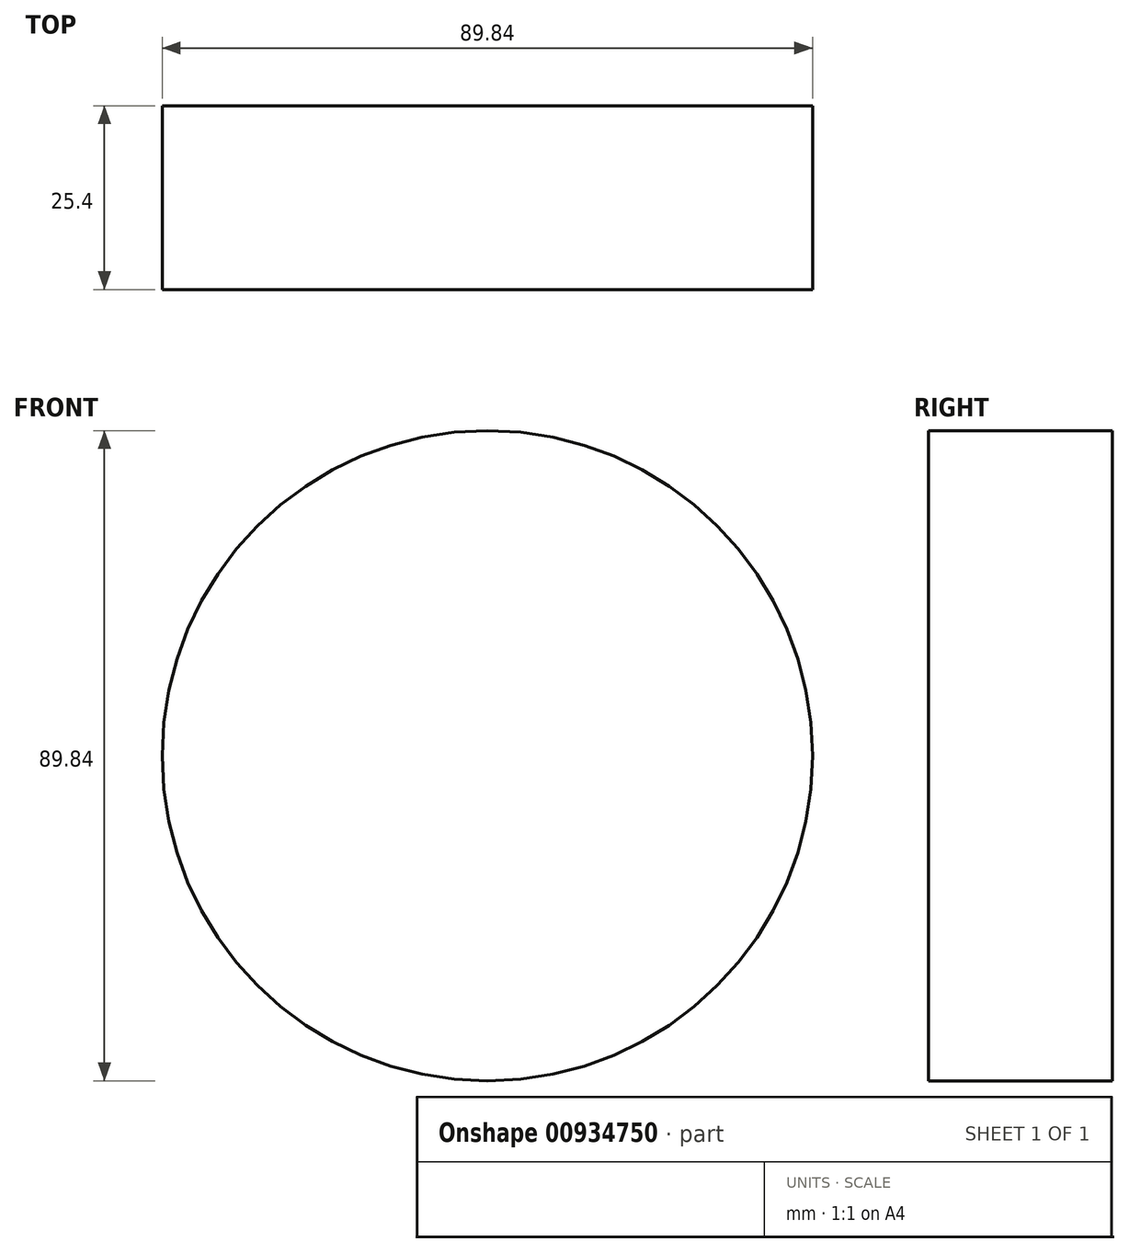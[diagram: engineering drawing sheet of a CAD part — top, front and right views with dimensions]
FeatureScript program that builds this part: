
annotation { "Feature Type Name" : "Feature", "Feature Type Description" : "" }
export const myFeature = defineFeature(function(context is Context, id is Id, definition is map)
    precondition{}
    {
        {
            var Q0;
            Q0=qCreatedBy(makeId("Front.planeOp"),FACE);
            var sketch = newSketch(context, id + "F0", { "sketchPlane" : qUnion([Q0])});
            skCircle(sketch, "E0", {"center": v(0, 0) * mm, "radius": 44.92 * mm});
            skSolve(sketch);
        }
        {
            var Q0;
            Q0 = qSketchRegion(id + "F0", true);
            extrude(context, id + "F1", {"entities" : qUnion([Q0]), "depth" : 25.4 * mm, "offsetDistance" : 25.4 * mm});
        }
    });
